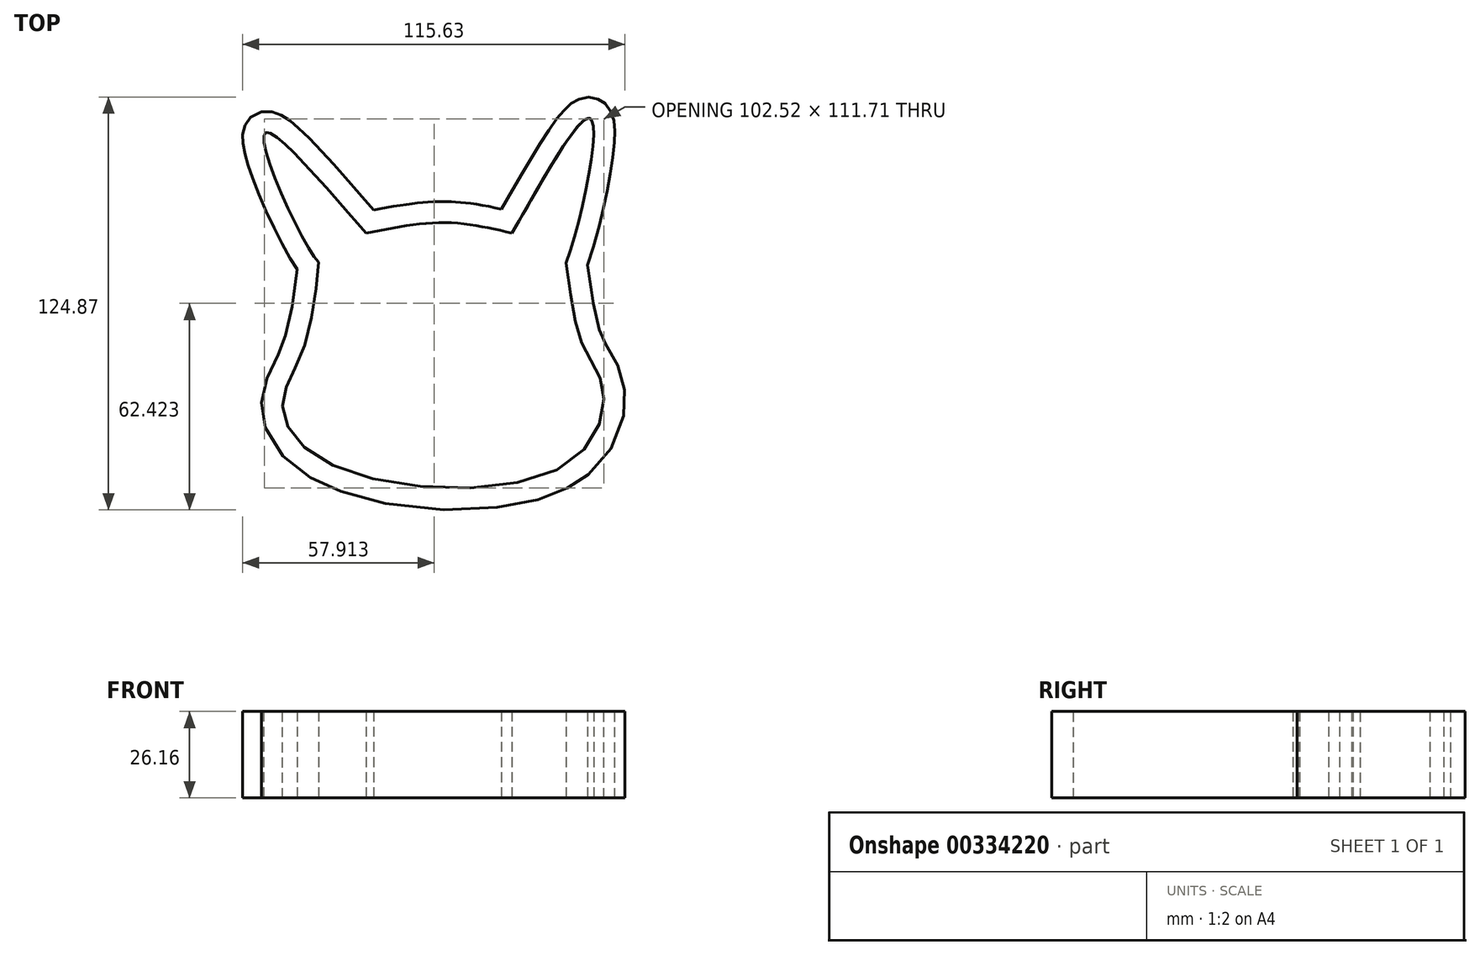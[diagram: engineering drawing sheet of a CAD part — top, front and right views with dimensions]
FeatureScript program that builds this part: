
annotation { "Feature Type Name" : "Feature", "Feature Type Description" : "" }
export const myFeature = defineFeature(function(context is Context, id is Id, definition is map)
    precondition{}
    {
        {
            var Q0;
            Q0=qCreatedBy(makeId("Top.planeOp"),FACE);
            var sketch = newSketch(context, id + "F0", { "sketchPlane" : qUnion([Q0])});
            skFitSpline(sketch, "E0", {"points": [v(-38.14, 11.53) * mm, v(-54.56, 50.44) * mm, v(-23.8, 20.34) * mm], "startDerivative": vector(-27.6, 25.76) * mm, "endDerivative": vector(54.75, -59.8) * mm});
            skFitSpline(sketch, "E1", {"points": [v(-23.8, 20.34) * mm, v(0, 23.53) * mm, v(20.23, 20.34) * mm], "startDerivative": vector(46.72, 9.45) * mm, "endDerivative": vector(41.26, -9.7) * mm});
            skFitSpline(sketch, "E2", {"points": [v(20.23, 20.34) * mm, v(43.9, 55.02) * mm, v(36.58, 11.37) * mm], "startDerivative": vector(47.28, 80.2) * mm, "endDerivative": vector(-28.7, -77.1) * mm});
            skFitSpline(sketch, "E3", {"points": [v(-38.14, 11.53) * mm, v(-43.28, -16) * mm, v(-49.07, -31.24) * mm, v(-35.03, -49.4) * mm, v(35.62, -50.3) * mm, v(47.85, -26.97) * mm, v(41.87, -13.98) * mm, v(36.58, 11.37) * mm], "startDerivative": vector(-12.64, -166.58) * mm, "endDerivative": vector(-37.73, 244.9) * mm});
            skFitSpline(sketch, "E4.0", {"points": [v(-44.48, 12) * mm, v(-44.6, 10.34) * mm, v(-44.93, 6.69) * mm, v(-45.57, 1.72) * mm, v(-46.23, -2.28) * mm, v(-46.8, -5.23) * mm, v(-47.45, -8.08) * mm, v(-48.06, -10.3) * mm, v(-48.58, -11.96) * mm, v(-48.99, -13.14) * mm, v(-49.4, -14.23) * mm, v(-49.85, -15.3) * mm, v(-50.33, -16.36) * mm, v(-51, -17.77) * mm, v(-51.87, -19.53) * mm, v(-52.95, -21.75) * mm, v(-53.99, -24.16) * mm, v(-54.73, -26.4) * mm, v(-55.15, -28.35) * mm, v(-55.37, -29.9) * mm, v(-55.45, -31.52) * mm, v(-55.4, -33.15) * mm, v(-55.2, -34.78) * mm, v(-54.75, -36.96) * mm, v(-53.85, -39.64) * mm, v(-52.25, -42.76) * mm, v(-50.13, -45.75) * mm, v(-47.53, -48.55) * mm, v(-44.44, -51.16) * mm, v(-41.46, -53.14) * mm, v(-38.84, -54.6) * mm, v(-36.06, -55.97) * mm, v(-32.33, -57.5) * mm, v(-27.52, -59.06) * mm, v(-20.7, -60.82) * mm, v(-11.58, -62.4) * mm, v(-0.12, -63.3) * mm, v(9.45, -63.16) * mm, v(16.87, -62.45) * mm, v(22.26, -61.61) * mm, v(27.43, -60.44) * mm, v(31.5, -59.16) * mm, v(34.6, -57.92) * mm, v(36.46, -57.06) * mm, v(37.9, -56.3) * mm, v(39.31, -55.5) * mm, v(41, -54.44) * mm, v(42.86, -53.06) * mm, v(45.15, -51.1) * mm, v(47.65, -48.46) * mm, v(50.07, -45.06) * mm, v(51.94, -41.53) * mm, v(53.27, -37.94) * mm, v(54.1, -34.36) * mm, v(54.41, -31.44) * mm, v(54.43, -29.15) * mm, v(54.35, -27.75) * mm, v(54.23, -26.65) * mm, v(54.06, -25.55) * mm, v(53.68, -23.7) * mm, v(52.91, -21.3) * mm, v(51.78, -18.78) * mm, v(50.59, -16.6) * mm, v(49.65, -15.02) * mm, v(48.96, -13.85) * mm, v(48.5, -13.02) * mm, v(48.07, -12.23) * mm, v(47.76, -11.6) * mm, v(47.53, -11.09) * mm, v(47.3, -10.56) * mm, v(47.03, -9.87) * mm, v(46.73, -8.99) * mm, v(46.33, -7.72) * mm, v(45.87, -5.98) * mm, v(45.36, -3.62) * mm, v(44.72, -0.1) * mm, v(43.95, 4.96) * mm, v(43.25, 9.75) * mm, v(42.86, 12.34) * mm]});
            skFitSpline(sketch, "E5.0", {"points": [v(-42.48, 6.88) * mm, v(-42.82, 7.2) * mm, v(-43.4, 7.82) * mm, v(-44.16, 8.76) * mm, v(-44.88, 9.75) * mm, v(-45.83, 11.17) * mm, v(-47.05, 13.15) * mm, v(-48.57, 15.85) * mm, v(-50.14, 18.83) * mm, v(-51.73, 22.02) * mm, v(-53.3, 25.36) * mm, v(-54.83, 28.76) * mm, v(-56.28, 32.17) * mm, v(-57.61, 35.5) * mm, v(-58.6, 38.17) * mm, v(-59.3, 40.21) * mm, v(-59.76, 41.7) * mm, v(-60.17, 43.12) * mm, v(-60.53, 44.5) * mm, v(-60.82, 45.83) * mm, v(-61.04, 47.15) * mm, v(-61.15, 48.27) * mm, v(-61.18, 49.23) * mm, v(-61.15, 50) * mm, v(-61.05, 50.85) * mm, v(-60.85, 51.82) * mm, v(-60.52, 52.75) * mm, v(-60.1, 53.56) * mm, v(-59.57, 54.4) * mm, v(-58.65, 55.45) * mm, v(-57.2, 56.44) * mm, v(-55.65, 57.02) * mm, v(-54.2, 57.23) * mm, v(-52.98, 57.18) * mm, v(-51.96, 57) * mm, v(-51.1, 56.75) * mm, v(-50.11, 56.37) * mm, v(-49.08, 55.84) * mm, v(-47.98, 55.15) * mm, v(-46.94, 54.4) * mm, v(-45.9, 53.58) * mm, v(-44.87, 52.7) * mm, v(-43.46, 51.42) * mm, v(-41.64, 49.67) * mm, v(-39.36, 47.33) * mm, v(-36.99, 44.8) * mm, v(-34.56, 42.15) * mm, v(-32.11, 39.4) * mm, v(-29.68, 36.64) * mm, v(-26.5, 33) * mm, v(-22.75, 28.68) * mm, v(-20.2, 25.82) * mm, v(-19.11, 24.63) * mm]});
            skFitSpline(sketch, "E6.0", {"points": [v(-25.06, 26.56) * mm, v(-23.1, 26.96) * mm, v(-19.17, 27.75) * mm, v(-14.16, 28.65) * mm, v(-10.11, 29.23) * mm, v(-7.06, 29.58) * mm, v(-4, 29.8) * mm, v(-1.43, 29.89) * mm, v(0.64, 29.87) * mm, v(2.68, 29.8) * mm, v(5.17, 29.62) * mm, v(8.1, 29.27) * mm, v(11.9, 28.68) * mm, v(16.46, 27.75) * mm, v(19.96, 26.93) * mm, v(21.68, 26.52) * mm]});
            skFitSpline(sketch, "E7.0", {"points": [v(14.76, 23.57) * mm, v(15.72, 25.2) * mm, v(17.82, 28.84) * mm, v(20.71, 33.89) * mm, v(23.1, 38.01) * mm, v(24.9, 41.1) * mm, v(26.7, 44.12) * mm, v(28.49, 47.02) * mm, v(30.24, 49.77) * mm, v(31.94, 52.32) * mm, v(33.31, 54.24) * mm, v(34.4, 55.65) * mm, v(35.21, 56.64) * mm, v(36.04, 57.57) * mm, v(36.9, 58.45) * mm, v(37.84, 59.3) * mm, v(38.76, 59.98) * mm, v(39.65, 60.5) * mm, v(40.44, 60.88) * mm, v(41.37, 61.21) * mm, v(42.5, 61.45) * mm, v(43.84, 61.51) * mm, v(45.08, 61.33) * mm, v(46.07, 61) * mm, v(46.78, 60.69) * mm, v(47.45, 60.3) * mm, v(48.23, 59.72) * mm, v(49.01, 58.94) * mm, v(49.68, 58.02) * mm, v(50.15, 57.17) * mm, v(50.6, 56.12) * mm, v(50.92, 54.95) * mm, v(51.14, 53.66) * mm, v(51.26, 52.4) * mm, v(51.3, 51.14) * mm, v(51.3, 49.84) * mm, v(51.23, 48.04) * mm, v(51.04, 45.65) * mm, v(50.66, 42.56) * mm, v(50.17, 39.28) * mm, v(49.57, 35.84) * mm, v(48.87, 32.3) * mm, v(48.1, 28.71) * mm, v(47.26, 25.13) * mm, v(46.07, 20.43) * mm, v(44.49, 14.83) * mm, v(43.19, 10.92) * mm, v(42.53, 9.16) * mm]});
            skSolve(sketch);
        }
        {
            var Q0;
            Q0=makeQuery(id+"F0.imprint","IMPRINT",FACE,{"disambiguationData":[TD([[makeQuery(id+"F0.imprint","IMPRINT",EDGE,{"derivedFrom":sQuery(id+"F0.wireOp",EDGE,"E0")}),1.0]])]});
            extrude(context, id + "F1", {"entities" : qUnion([Q0]), "depth" : 26.16 * mm});
        }
    });
